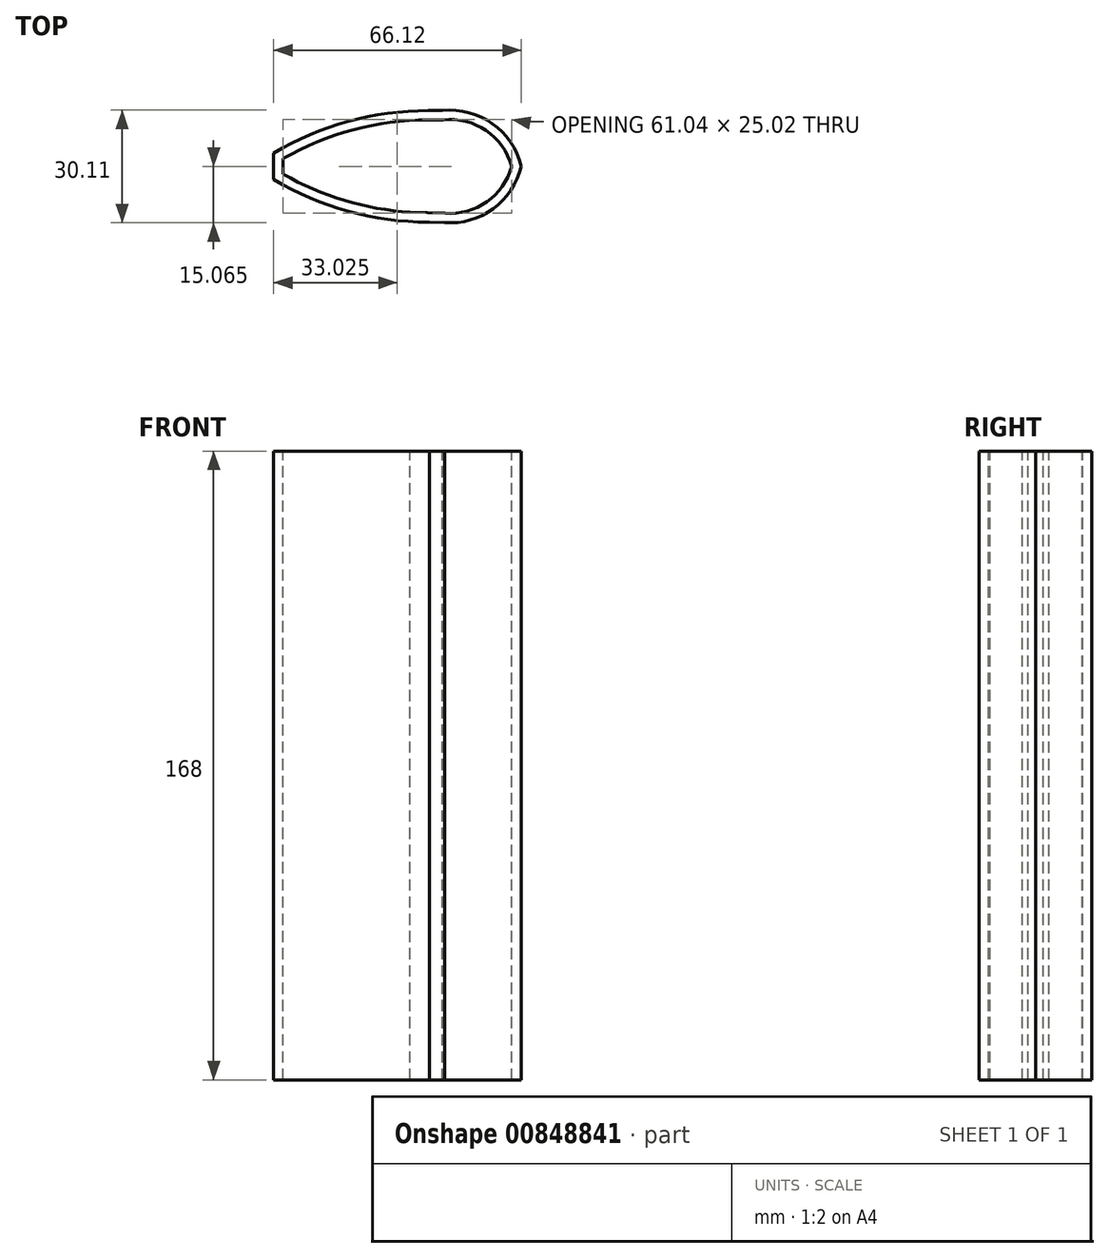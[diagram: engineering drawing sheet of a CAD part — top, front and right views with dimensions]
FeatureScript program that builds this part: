
annotation { "Feature Type Name" : "Feature", "Feature Type Description" : "" }
export const myFeature = defineFeature(function(context is Context, id is Id, definition is map)
    precondition{}
    {
        {
            var Q0;
            Q0=qCreatedBy(makeId("Top.planeOp"),FACE);
            var sketch = newSketch(context, id + "F0", { "sketchPlane" : qUnion([Q0])});
            skLineSegment(sketch, "E0", {"start": v(-29.7, 0) * mm, "end": v(-29.7, 2.07) * mm});
            skLineSegment(sketch, "E1", {"start": v(-29.7, 0) * mm, "end": v(-29.7, -2.07) * mm});
            skArc(sketch, "E2", {"start": v(9.03, 12.4) * mm, "mid": v(-11, 9.75) * mm, "end": v(-29.7, 2.07) * mm});
            skArc(sketch, "E3", {"start": v(-29.7, -2.07) * mm, "mid": v(-13.32, -9.1) * mm, "end": v(4.22, -12.25) * mm});
            skArc(sketch, "E4", {"start": v(31.35, 0) * mm, "mid": v(24.48, 9.6) * mm, "end": v(13.03, 12.4) * mm});
            skLineSegment(sketch, "E5", {"start": v(9.03, 12.4) * mm, "end": v(13.03, 12.4) * mm});
            skLineSegment(sketch, "E6", {"start": v(4.22, -12.25) * mm, "end": v(13.55, -12.53) * mm});
            skArc(sketch, "E7.MirrorCS", {"start": v(31.35, 0) * mm, "mid": v(24.72, -9.49) * mm, "end": v(13.55, -12.53) * mm});
            skLineSegment(sketch, "E8.bottom", {"start": v(-239.36, 34.93) * mm, "end": v(88.89, 34.93) * mm, "construction": true});
            skLineSegment(sketch, "E8.top", {"start": v(-239.36, -35.07) * mm, "end": v(88.89, -35.07) * mm, "construction": true});
            skLineSegment(sketch, "E8.left", {"start": v(-239.36, 34.93) * mm, "end": v(-239.36, -35.07) * mm, "construction": true});
            skLineSegment(sketch, "E8.right", {"start": v(88.89, 34.93) * mm, "end": v(88.89, -35.07) * mm, "construction": true});
            skPoint(sketch, "E8.middle", {"position": v(-75.24, -0.07) * mm});
            skFitSpline(sketch, "E9.0", {"points": [v(-96.69, 34.83) * mm, v(-106.82, 36.01) * mm, v(-128.8, 36.75) * mm, v(-157.43, 33.2) * mm, v(-179.11, 27.35) * mm, v(-194.28, 21.34) * mm, v(-207.88, 13.59) * mm, v(-215.56, 7.14) * mm, v(-218.94, 3.57) * mm]});
            skFitSpline(sketch, "E10.0", {"points": [v(-96.69, -34.83) * mm, v(-106.82, -36.01) * mm, v(-128.8, -36.72) * mm, v(-157.44, -33.09) * mm, v(-179.12, -27.17) * mm, v(-194.3, -21.12) * mm, v(-207.89, -13.34) * mm, v(-215.56, -6.88) * mm, v(-218.94, -3.31) * mm]});
            skFitSpline(sketch, "E11", {"points": [v(-218.94, 3.57) * mm, v(-218.94, -3.31) * mm], "startDerivative": vector(-13.48, -10.86) * mm, "endDerivative": vector(13.66, -9.93) * mm});
            skLineSegment(sketch, "E12.0", {"start": v(9.45, 14.9) * mm, "end": v(12.9, 14.9) * mm});
            skArc(sketch, "E12.1", {"start": v(33.92, 0) * mm, "mid": v(26.22, 11.43) * mm, "end": v(12.9, 14.9) * mm});
            skArc(sketch, "E12.2", {"start": v(9.45, 14.9) * mm, "mid": v(-12.15, 12.03) * mm, "end": v(-32.2, 3.5) * mm});
            skArc(sketch, "E12.3", {"start": v(33.92, 0) * mm, "mid": v(26.46, -11.31) * mm, "end": v(13.42, -15.03) * mm});
            skLineSegment(sketch, "E12.4", {"start": v(-32.2, 0) * mm, "end": v(-32.2, 3.5) * mm});
            skLineSegment(sketch, "E12.5", {"start": v(-32.2, 0) * mm, "end": v(-32.2, -3.5) * mm});
            skArc(sketch, "E12.6", {"start": v(-32.2, -3.5) * mm, "mid": v(-12.15, -12.03) * mm, "end": v(9.45, -14.9) * mm});
            skLineSegment(sketch, "E12.7", {"start": v(9.45, -14.9) * mm, "end": v(13.42, -15.03) * mm});
            skLineSegment(sketch, "E13", {"start": v(-29.7, -2.07) * mm, "end": v(-29.7, -43.83) * mm, "construction": true});
            skFitSpline(sketch, "E14", {"points": [v(-97.3, 34.9) * mm, v(9.45, 14.9) * mm], "startDerivative": vector(182.69, -15.15) * mm, "endDerivative": vector(184.3, 0.06) * mm});
            skFitSpline(sketch, "E15.MirrorCS", {"points": [v(-97.3, -34.9) * mm, v(9.45, -14.9) * mm], "startDerivative": vector(182.69, 15.15) * mm, "endDerivative": vector(184.3, -0.06) * mm});
            skLineSegment(sketch, "E16", {"start": v(18.2, 19.76) * mm, "end": v(18.2, -21.37) * mm, "construction": true});
            skSolve(sketch);
        }
        {
            var Q0;
            Q0=makeQuery(id+"F0.imprint","IMPRINT",FACE,{"disambiguationData":[TD([[makeQuery(id+"F0.imprint","IMPRINT",EDGE,{"derivedFrom":sQuery(id+"F0.wireOp",EDGE,"5e83ef56-0208-4088-b49c-41c91eda866b.0")}),-1.0]])]});
            var Q1;
            Q1=makeQuery(id+"F0.imprint","IMPRINT",FACE,{"disambiguationData":[TD([[makeQuery(id+"F0.imprint","IMPRINT",EDGE,{"derivedFrom":sQuery(id+"F0.wireOp",EDGE,"E0")}),1.0]])]});
            var Q2;
            {var subQ3=sQuery(id+"F0.wireOp",EDGE,"928a92dc-c077-4a9c-8fc9-b773f015ef270.MirrorCS");Q2=makeQuery(id+"F0.imprint","IMPRINT",FACE,{"disambiguationData":[TD([[makeQuery(id+"F0.imprint","IMPRINT",EDGE,{"derivedFrom":subQ3}),1.0]])]});}
            extrude(context, id + "F1", {"entities" : qUnion([Q0, Q1, Q2]), "oppositeDirection" : true, "depth" : 168 * mm, "offsetDistance" : 25 * mm});
        }
    });
